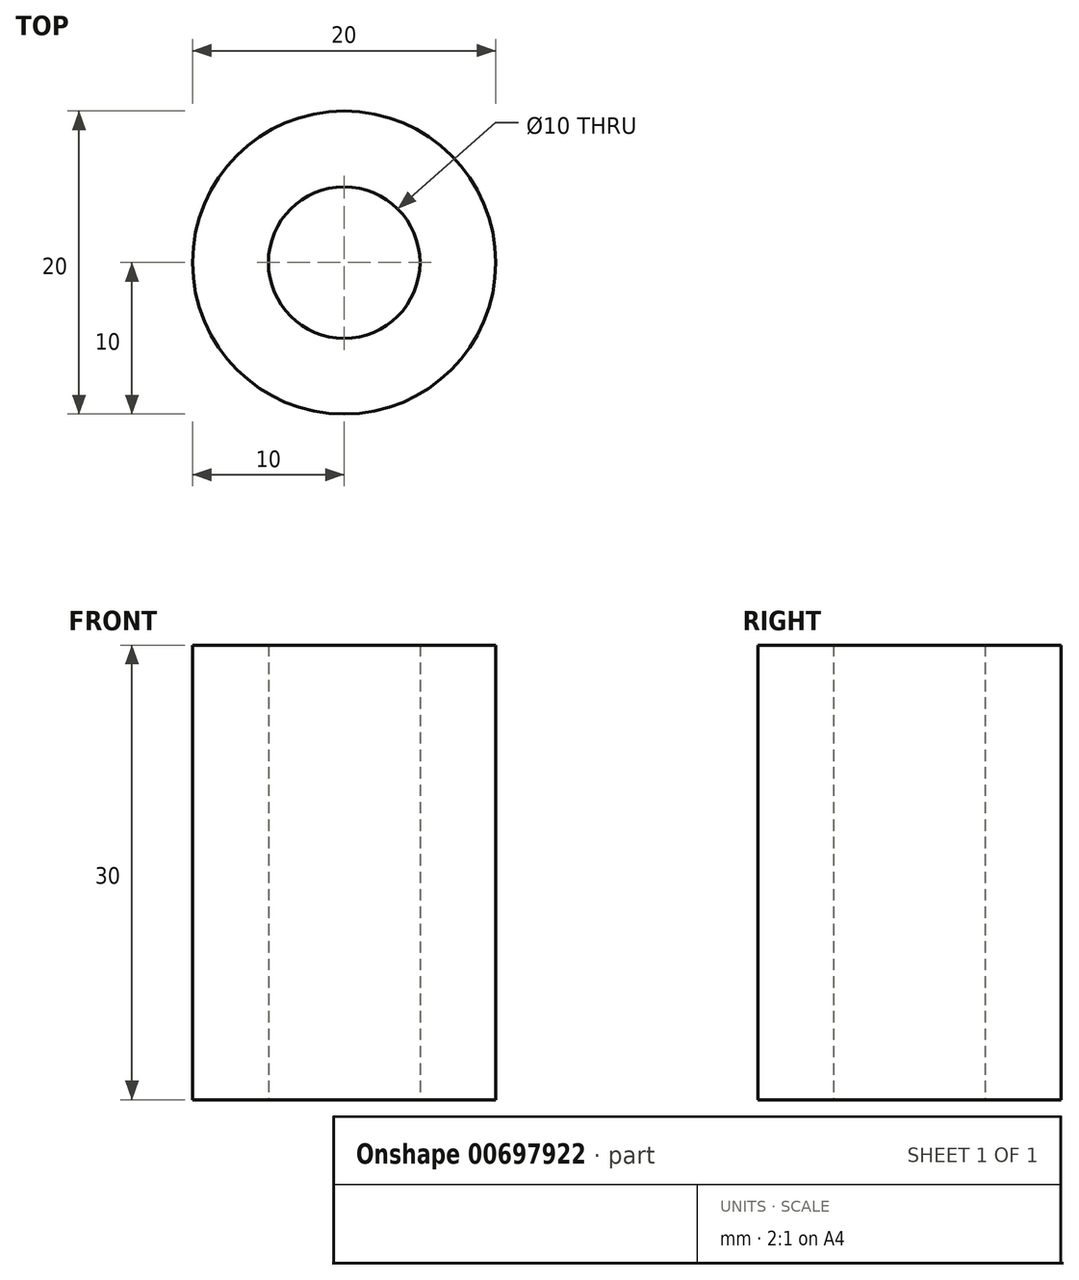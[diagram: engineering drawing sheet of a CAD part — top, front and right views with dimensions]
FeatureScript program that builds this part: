
annotation { "Feature Type Name" : "Feature", "Feature Type Description" : "" }
export const myFeature = defineFeature(function(context is Context, id is Id, definition is map)
    precondition{}
    {
        {
            var Q0;
            Q0=qCreatedBy(makeId("Top.planeOp"),FACE);
            var sketch = newSketch(context, id + "F0", { "sketchPlane" : qUnion([Q0])});
            skCircle(sketch, "E0", {"center": v(0, 0) * mm, "radius": 10 * mm});
            skCircle(sketch, "E1", {"center": v(0, 0) * mm, "radius": 5 * mm});
            skSolve(sketch);
        }
        {
            var Q0;
            Q0=makeQuery(id+"F0.imprint","IMPRINT",FACE,{"disambiguationData":[TD([[makeQuery(id+"F0.imprint","IMPRINT",EDGE,{"derivedFrom":sQuery(id+"F0.wireOp",EDGE,"E0")}),1.0]])]});
            extrude(context, id + "F1", {"entities" : qUnion([Q0]), "depth" : 30 * mm, "offsetDistance" : 25 * mm});
        }
    });
